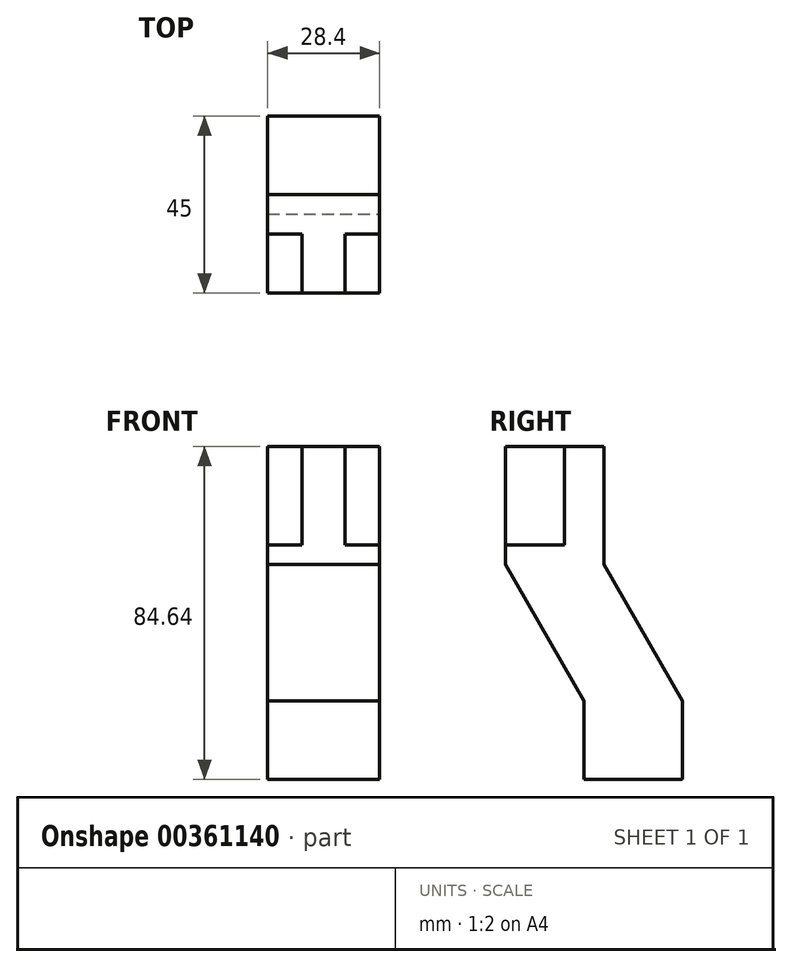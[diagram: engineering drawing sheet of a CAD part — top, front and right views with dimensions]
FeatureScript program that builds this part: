
annotation { "Feature Type Name" : "Feature", "Feature Type Description" : "" }
export const myFeature = defineFeature(function(context is Context, id is Id, definition is map)
    precondition{}
    {
        {
            var Q0;
            Q0=qCreatedBy(makeId("Top.planeOp"),FACE);
            var sketch = newSketch(context, id + "F0", { "sketchPlane" : qUnion([Q0])});
            skLineSegment(sketch, "E0", {"start": v(-5.5, -12.5) * mm, "end": v(5.5, -12.5) * mm});
            skLineSegment(sketch, "E1", {"start": v(5.5, -12.5) * mm, "end": v(5.5, 2.5) * mm});
            skLineSegment(sketch, "E2", {"start": v(5.5, 2.5) * mm, "end": v(14.2, 2.5) * mm});
            skLineSegment(sketch, "E3", {"start": v(14.2, 2.5) * mm, "end": v(14.2, 12.5) * mm});
            skLineSegment(sketch, "E4", {"start": v(14.2, 12.5) * mm, "end": v(-14.2, 12.5) * mm});
            skLineSegment(sketch, "E5", {"start": v(-14.2, 12.5) * mm, "end": v(-14.2, 2.5) * mm});
            skLineSegment(sketch, "E6", {"start": v(-14.2, 2.5) * mm, "end": v(-5.5, 2.5) * mm});
            skLineSegment(sketch, "E7", {"start": v(-5.5, 2.5) * mm, "end": v(-5.5, -12.5) * mm});
            skSolve(sketch);
        }
        {
            var Q0;
            Q0=makeQuery(id+"F0.imprint","IMPRINT",FACE,{"disambiguationData":[TD([[makeQuery(id+"F0.imprint","IMPRINT",EDGE,{"derivedFrom":sQuery(id+"F0.wireOp",EDGE,"E0")}),1.0]])]});
            extrude(context, id + "F1", {"entities" : qUnion([Q0]), "oppositeDirection" : true, "depth" : 25 * mm});
        }
        {
            var Q0;
            Q0=makeQuery(id+"F1.opExtrude","CAP_FACE",FACE,{"disambiguationData":[OSD([sQuery(id+"F0.wireOp",EDGE,"E0"),sQuery(id+"F0.wireOp",EDGE,"E1"),sQuery(id+"F0.wireOp",EDGE,"E2"),sQuery(id+"F0.wireOp",EDGE,"E3"),sQuery(id+"F0.wireOp",EDGE,"E4"),sQuery(id+"F0.wireOp",EDGE,"E5"),sQuery(id+"F0.wireOp",EDGE,"E6"),sQuery(id+"F0.wireOp",EDGE,"E7")])],"isStart":false});
            var sketch = newSketch(context, id + "F2", { "sketchPlane" : qUnion([Q0])});
            skLineSegment(sketch, "E8.bottom", {"start": v(-14.2, 12.5) * mm, "end": v(14.2, 12.5) * mm});
            skLineSegment(sketch, "E8.top", {"start": v(-14.2, -12.5) * mm, "end": v(14.2, -12.5) * mm});
            skLineSegment(sketch, "E8.left", {"start": v(-14.2, 12.5) * mm, "end": v(-14.2, -12.5) * mm});
            skLineSegment(sketch, "E8.right", {"start": v(14.2, 12.5) * mm, "end": v(14.2, -12.5) * mm});
            skSolve(sketch);
        }
        {
            var Q0;
            Q0 = qSketchRegion(id + "F2", true);
            extrude(context, id + "F3", {"entities" : qUnion([Q0]), "operationType" : NewBodyOperationType.ADD, "depth" : 5 * mm});
        }
        {
            var Q0;
            Q0=makeQuery(id+"F3.boolean.opBoolean","MERGE",FACE,{"derivedFrom":[makeQuery(id+"F1.opExtrude","SWEPT_FACE",FACE,{"disambiguationData":[OSD([sQuery(id+"F0.wireOp",EDGE,"E3")])]}),makeQuery(id+"F3.opExtrude","SWEPT_FACE",FACE,{"disambiguationData":[OSD([sQuery(id+"F2.wireOp",EDGE,"E8.right")])]})]});
            var sketch = newSketch(context, id + "F4", { "sketchPlane" : qUnion([Q0])});
            skLineSegment(sketch, "E9", {"start": v(12.5, -30) * mm, "end": v(-12.5, -30) * mm});
            skLineSegment(sketch, "E10", {"start": v(-12.5, -30) * mm, "end": v(7.5, -64.64) * mm});
            skLineSegment(sketch, "E11", {"start": v(7.5, -64.64) * mm, "end": v(7.5, -84.64) * mm});
            skLineSegment(sketch, "E12", {"start": v(7.5, -84.64) * mm, "end": v(32.5, -84.64) * mm});
            skLineSegment(sketch, "E13", {"start": v(32.5, -84.64) * mm, "end": v(32.5, -64.64) * mm});
            skLineSegment(sketch, "E14", {"start": v(32.5, -64.64) * mm, "end": v(12.5, -30) * mm});
            skSolve(sketch);
        }
        {
            var Q0;
            Q0=makeQuery(id+"F4.imprint","IMPRINT",FACE,{"disambiguationData":[TD([[makeQuery(id+"F4.imprint","IMPRINT",EDGE,{"derivedFrom":sQuery(id+"F4.wireOp",EDGE,"E9")}),-1.0]])]});
            extrude(context, id + "F5", {"entities" : qUnion([Q0]), "operationType" : NewBodyOperationType.ADD, "oppositeDirection" : true, "depth" : 28.4 * mm});
        }
    });
